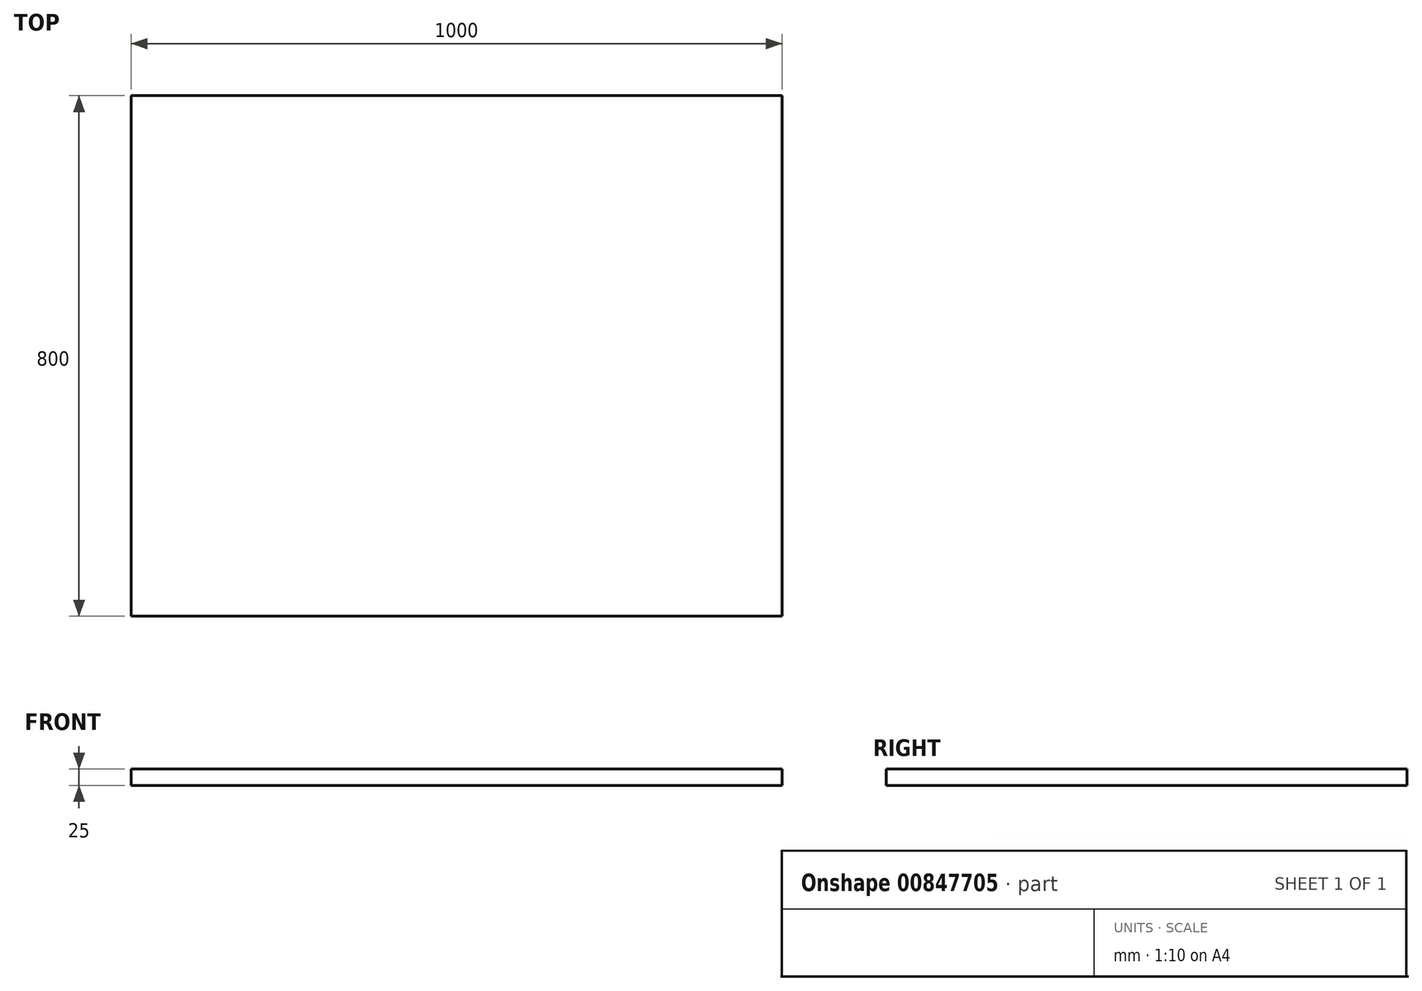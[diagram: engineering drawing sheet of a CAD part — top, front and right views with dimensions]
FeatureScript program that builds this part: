
annotation { "Feature Type Name" : "Feature", "Feature Type Description" : "" }
export const myFeature = defineFeature(function(context is Context, id is Id, definition is map)
    precondition{}
    {
        {
            var Q0;
            Q0=qCreatedBy(makeId("Top.planeOp"),FACE);
            var sketch = newSketch(context, id + "F0", { "sketchPlane" : qUnion([Q0])});
            skLineSegment(sketch, "E0.bottom", {"start": v(0, 0) * mm, "end": v(-1000, 0) * mm});
            skLineSegment(sketch, "E0.top", {"start": v(0, 800) * mm, "end": v(-1000, 800) * mm});
            skLineSegment(sketch, "E0.left", {"start": v(0, 0) * mm, "end": v(0, 800) * mm});
            skLineSegment(sketch, "E0.right", {"start": v(-1000, 0) * mm, "end": v(-1000, 800) * mm});
            skSolve(sketch);
        }
        {
            var Q0;
            Q0=makeQuery(id+"F0.imprint","IMPRINT",FACE,{"disambiguationData":[TD([[makeQuery(id+"F0.imprint","IMPRINT",EDGE,{"derivedFrom":sQuery(id+"F0.wireOp",EDGE,"E0.bottom")}),-1.0]])]});
            extrude(context, id + "F1", {"entities" : qUnion([Q0]), "depth" : 25 * mm, "offsetDistance" : 25 * mm});
        }
    });
